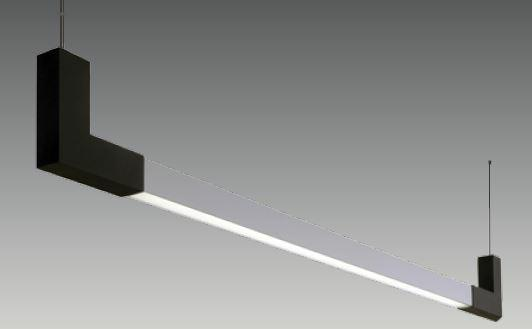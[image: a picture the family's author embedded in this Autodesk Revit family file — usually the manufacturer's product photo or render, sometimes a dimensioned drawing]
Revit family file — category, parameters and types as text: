
# Revit family: S 1800 PLU
name_source: partatom
category: Lighting Fixtures
revit_build: Autodesk Revit 2017 (Build: 20160225_1515(x64)
units: mm (PartAtom-declared; Revit-internal decimal feet)

## family parameters
Cut with Voids When Loaded = No
Host = Face
Light Source = Yes
Part Type = Normal
Room Calculation Point = No
Round Connector Dimension = Use Diameter
Shared = No

## types (2) — shared parameters
Color Filter = 16777215
Default Elevation = 1219 mm
Dimming Lamp Color Temperature Shift = <None>
Emit Shape Visible in Rendering = Yes
Emit from Rectangle Length = 40 mm  [stored 0.131234 ft]
Emit from Rectangle Width = 1410 mm  [stored 4.62598 ft]
Light Source Symbol Size = 610 mm
Manufacturer = ARLIGHT
Type Image = S 1800 PLU.JPG
Wattage Comments = 54W

## per-type parameters (varying)
| type | Apparent Load |
| SPLU.1800.54.30 | 0 VA |
| SPLU.1800.54.40 | 54 VA |

note: [stored X ft] marks values corroborated as IEEE doubles in the binary element streams (Revit-internal decimal feet)

## geometry (parser evidence)
native form markers: Sweep x3
no freeform markers — native parametric forms only
